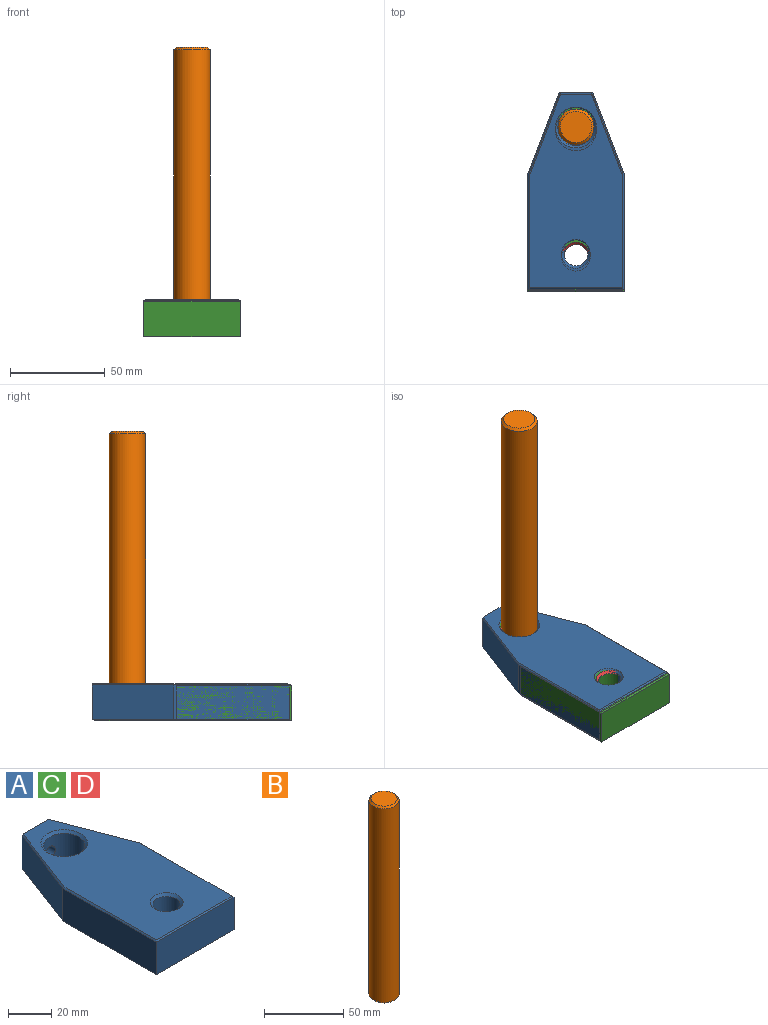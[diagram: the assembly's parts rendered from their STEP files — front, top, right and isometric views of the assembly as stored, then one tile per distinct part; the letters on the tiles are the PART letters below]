
ASSEMBLY  parts=4 mates=1
PART A: 20 faces, bbox 50.8x104.1x19 mm
  f0: plane 50.8x18.36mm, normal (0,-1,0), area 932.9mm2, adj f1,f5,f7,f18
  f1: plane 60.96x18.36mm, normal (1,0,0), area 1119.5mm2, adj f0,f2,f7,f17
  f2: plane 43.18x18.36mm, normal (0.93,0.36,0), area 849mm2, adj f1,f3,f7,f15
  f3: plane 19x17.78mm, normal (0,1,0), area 305.7mm2, adj f2,f4,f6,f7,f14,f15,f19
  f4: plane 43.18x18.36mm, normal (-0.93,0.36,0), area 849mm2, adj f3,f5,f7,f14
  f5: plane 60.96x18.36mm, normal (-1,0,0), area 1119.5mm2, adj f0,f4,f7,f16
  f6: plane 103.51x49.53mm, normal (0,0,1), area 3861.3mm2, adj f3,f12,f13,f14,f15,f16,f17,f18
  f7: plane 104.14x50.8mm, normal (0,0,-1), area 4028.9mm2, adj f0,f1,f2,f3,f4,f5,f10,f11
  f8: cylinder r=9.53mm len=19.05mm, axis (0,0,-1), area 952.9mm2, adj f10,f12,f19
  f9: cylinder r=6.35mm len=16.46mm, axis (0,0,-1), area 656.7mm2, adj f11,f13
  f10: cone r=10.79mm half-angle=45deg, axis (0,0,-1), area 114.7mm2, adj f7,f8
  f11: cone r=7.62mm half-angle=45deg, axis (0,0,-1), area 78.8mm2, adj f7,f9
  f12: cone r=10.79mm half-angle=45deg, axis (0,0,1), area 114.7mm2, adj f6,f8
  f13: cone r=7.62mm half-angle=45deg, axis (0,0,1), area 78.8mm2, adj f6,f9
  f14: plane 43.3x17.19mm, normal (-0.66,0.25,0.71), area 41.6mm2, adj f3,f4,f6,f16
  f15: plane 43.3x17.19mm, normal (0.66,0.25,0.71), area 41.6mm2, adj f2,f3,f6,f17
  f16: plane 60.96x0.64mm, normal (-0.71,0,0.71), area 54.4mm2, adj f5,f6,f14,f18
  f17: plane 60.96x0.64mm, normal (0.71,0,0.71), area 54.4mm2, adj f1,f6,f15,f18
  f18: plane 50.8x0.64mm, normal (0,-0.71,0.71), area 45mm2, adj f0,f6,f16,f17
  f19: cylinder r=3.17mm len=9.74mm, axis (0,1,0), area 188.7mm2, adj f3,f8
PART B: 5 faces, bbox 19.1x19.1x152.4 mm
  f0: cylinder r=9.53mm len=149.86mm, axis (0,0,-1), area 8968.7mm2, adj f3,f4
  f1: plane 16.51x16.51mm, normal (0,0,1), area 214.1mm2, adj f3
  f2: plane 16.51x16.51mm, normal (0,0,-1), area 214.1mm2, adj f4
  f3: cone r=8.26mm half-angle=45deg, axis (0,0,-1), area 100.3mm2, adj f0,f1
  f4: cone r=9.53mm half-angle=45deg, axis (0,0,1), area 100.3mm2, adj f0,f2
PART C: same geometry as A
PART D: same geometry as A
PLACE A t=(0,1.48,0.49)mm
PLACE B rot(axis=(0.71,-0.71,0),180deg) t=(79.09,48.37,152.89)mm
PLACE C at identity
PLACE D at identity
MATE slider B.f0 <-> A.f8  axis (0,0,-1) through (42.73,96.66,1.76)mm
